# Revit family: AFX-Axel_Vanity-
name_source: partatom
category: Lighting Fixtures
units: mm (PartAtom-declared; Revit-internal decimal feet)

## family parameters
Cut with Voids When Loaded = No
Host = Face
Light Source = Yes
Part Type = Normal
Room Calculation Point = No
Round Connector Dimension = Use Diameter
Shared = No

## types (10) — shared parameters
Apparent Load = 0 VA
Assembly Code = D5020200
Cap Finish = AFX - Black Steel
Color Filter = 16777215
Colour Rendering Index = 90
Default Elevation = 48"
Depth = 4 3/16"
Diffuser Finish = AFX - White Acrylic
Dimming Lamp Color Temperature Shift = <None>
Frame Finish = AFX - Black Steel
Height = 4 1/8"
Keynote = 12500
Manufacturer = AFX Inc
Product Documentation Link = https://www.afxinc.com
Revit File Built By = https://servex-us.com
Screen Finish = AFX - White Acrylic
Support Finish = AFX - Black Steel
Tilt Angle = 0.00°
Type Comments = Axel
URL = https://www.afxinc.com
Voltage = 120 V

## per-type parameters (varying)
| type | Description | LED Finish | Length | Photometric Web File | Wattage Comments |
| AXLV2404LAJUDBK-3000K | Timeless contemporary design LED vanity with vertical or horizontal mounting -3000K- 24 3/4"L x 4"D x 4 1/8"H | AFX - White Plastic | 24 3/4" | AXLV2404LAJUDBK SN SB_3000K_IES.IES | 25 |
| AXLV3604LAJUDBK-3000K | Timeless contemporary design LED vanity with vertical or horizontal mounting -3000K- 36 3/4"L x 4"D x 4 1/8"H | AFX - White Acrylic | 36 3/4" | AXLV3604LAJUDBK SN SB_3000K_IES.IES | 30 |
| AXLV2404LAJUDBK-2700K | Timeless contemporary design LED vanity with vertical or horizontal mounting -2700K- 24 3/4"L x 4"D x 4 1/8"H | AFX - White Plastic | 24 3/4" | AXLV2404LAJUDBK SN SB_2700K_IES.IES | 25 |
| AXLV2404LAJUDBK-3500K | Timeless contemporary design LED vanity with vertical or horizontal mounting -3500K- 24 3/4"L x 4"D x 4 1/8"H | AFX - White Plastic | 24 3/4" | AXLV2404LAJUDBK SN SB_3500K_IES.IES | 25 |
| AXLV2404LAJUDBK-4000K | Timeless contemporary design LED vanity with vertical or horizontal mounting -4000K- 24 3/4"L x 4"D x 4 1/8"H | AFX - White Plastic | 24 3/4" | AXLV2404LAJUDBK SN SB_4000K_IES.IES | 25 |
| AXLV2404LAJUDBK-5000K | Timeless contemporary design LED vanity with vertical or horizontal mounting -5000K- 24 3/4"L x 4"D x 4 1/8"H | AFX - White Plastic | 24 3/4" | AXLV2404LAJUDBK SN SB_5000K_IES.IES | 25 |
| AXLV3604LAJUDBK-2700K | Timeless contemporary design LED vanity with vertical or horizontal mounting -2700K- 36 3/4"L x 4"D x 4 1/8"H | AFX - White Acrylic | 36 3/4" | AXLV3604LAJUDBK SN SB_2700K_IES.IES | 30 |
| AXLV3604LAJUDBK-3500K | Timeless contemporary design LED vanity with vertical or horizontal mounting -3500K- 36 3/4"L x 4"D x 4 1/8"H | AFX - White Acrylic | 36 3/4" | AXLV3604LAJUDBK SN SB_3500K_IES.IES | 30 |
| AXLV3604LAJUDBK-4000K | Timeless contemporary design LED vanity with vertical or horizontal mounting -4000K- 36 3/4"L x 4"D x 4 1/8"H | AFX - White Acrylic | 36 3/4" | AXLV3604LAJUDBK SN SB_4000K_IES.IES | 30 |
| AXLV3604LAJUDBK-5000K | Timeless contemporary design LED vanity with vertical or horizontal mounting -5000K- 36 3/4"L x 4"D x 4 1/8"H | AFX - White Acrylic | 36 3/4" | AXLV3604LAJUDBK SN SB_5000K_IES.IES | 30 |

note: column(s) folded — value = type name in every type: Model

## geometry (parser evidence)
native form markers: Sweep x3
no freeform markers — native parametric forms only
